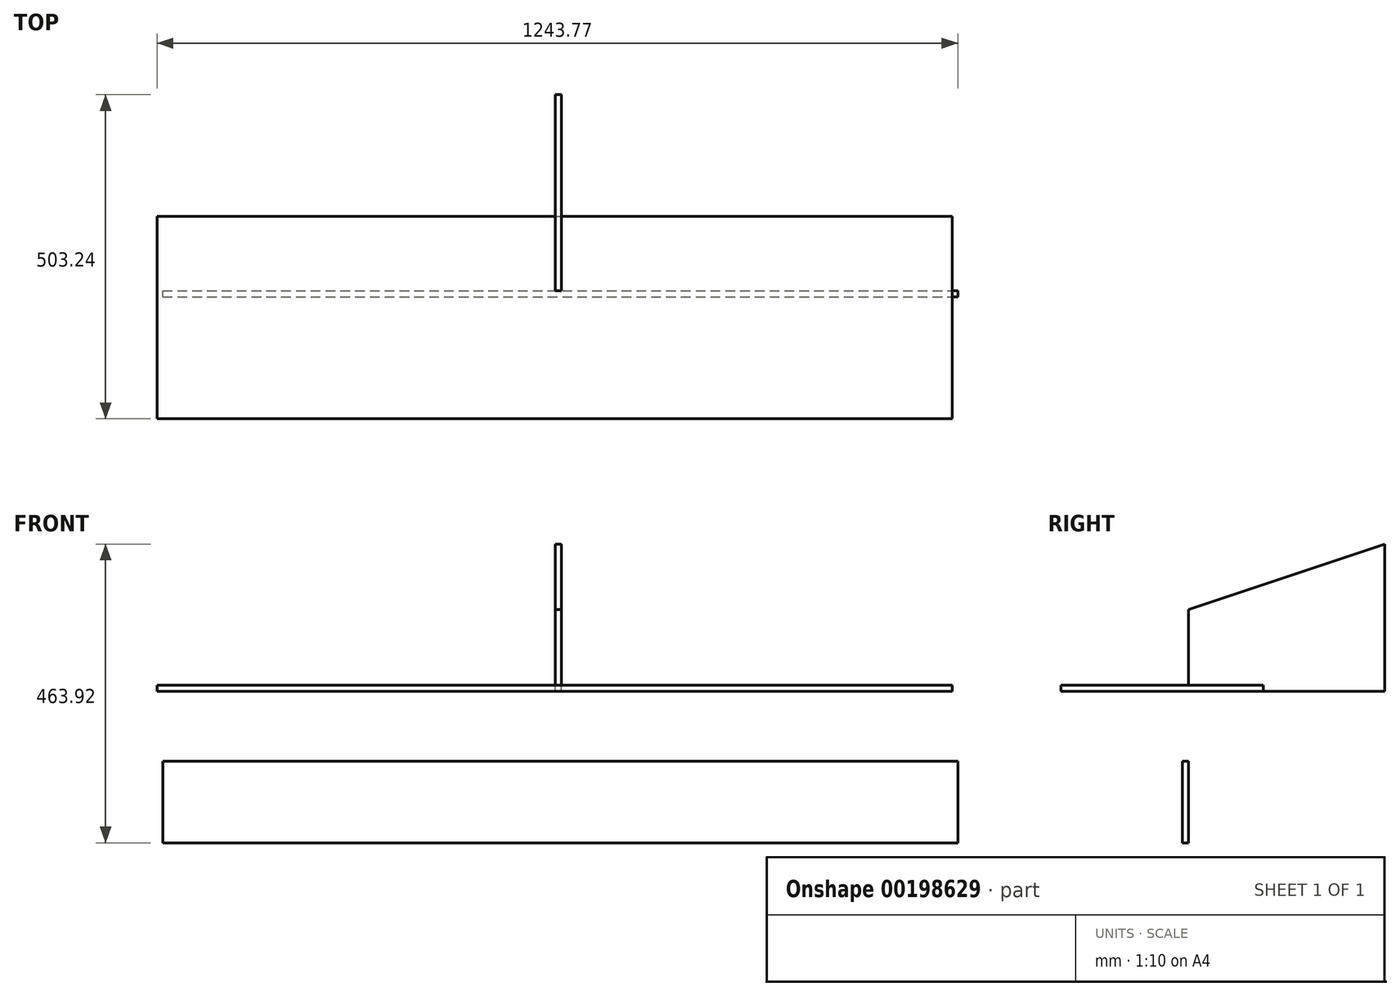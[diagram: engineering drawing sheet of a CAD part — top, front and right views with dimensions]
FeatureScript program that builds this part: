
annotation { "Feature Type Name" : "Feature", "Feature Type Description" : "" }
export const myFeature = defineFeature(function(context is Context, id is Id, definition is map)
    precondition{}
    {
        {
            var Q0;
            Q0=qCreatedBy(makeId("Right.planeOp"),FACE);
            var sketch = newSketch(context, id + "F0", { "sketchPlane" : qUnion([Q0])});
            skLineSegment(sketch, "E0", {"start": v(0, 0) * mm, "end": v(0, 127) * mm});
            skLineSegment(sketch, "E1", {"start": v(0, 0) * mm, "end": v(304.8, 0) * mm});
            skLineSegment(sketch, "E2", {"start": v(304.8, 0) * mm, "end": v(304.8, 228.6) * mm});
            skLineSegment(sketch, "E3", {"start": v(304.8, 228.6) * mm, "end": v(0, 127) * mm});
            skSolve(sketch);
        }
        {
            var Q0;
            Q0 = qSketchRegion(id + "F0", true);
            extrude(context, id + "F1", {"entities" : qUnion([Q0]), "depth" : 9.52 * mm});
        }
        {
            var Q0;
            Q0=qCreatedBy(makeId("Front.planeOp"),FACE);
            var sketch = newSketch(context, id + "F2", { "sketchPlane" : qUnion([Q0])});
            skLineSegment(sketch, "E4.bottom", {"start": v(-609.63, -108.32) * mm, "end": v(625.45, -108.32) * mm});
            skLineSegment(sketch, "E4.top", {"start": v(-609.63, -235.32) * mm, "end": v(625.45, -235.32) * mm});
            skLineSegment(sketch, "E4.left", {"start": v(-609.63, -108.32) * mm, "end": v(-609.63, -235.32) * mm});
            skLineSegment(sketch, "E4.right", {"start": v(625.45, -108.32) * mm, "end": v(625.45, -235.32) * mm});
            skSolve(sketch);
        }
        {
            var Q0;
            Q0 = qSketchRegion(id + "F2", true);
            extrude(context, id + "F3", {"entities" : qUnion([Q0]), "depth" : 9.52 * mm});
        }
        {
            var Q0;
            Q0=qCreatedBy(makeId("Top.planeOp"),FACE);
            var sketch = newSketch(context, id + "F4", { "sketchPlane" : qUnion([Q0])});
            skLineSegment(sketch, "E5", {"start": v(-618.32, 115.89) * mm, "end": v(616.75, 115.89) * mm});
            skLineSegment(sketch, "E6", {"start": v(-618.32, 115.89) * mm, "end": v(-618.32, -198.44) * mm});
            skLineSegment(sketch, "E7", {"start": v(-618.32, -198.44) * mm, "end": v(616.75, -198.44) * mm});
            skLineSegment(sketch, "E8", {"start": v(616.75, -198.44) * mm, "end": v(616.75, 115.89) * mm});
            skLineSegment(sketch, "E9.0", {"start": v(-308.76, 115.89) * mm, "end": v(-308.76, -198.44) * mm});
            skLineSegment(sketch, "E10.0", {"start": v(0.8, 115.89) * mm, "end": v(0.8, -198.44) * mm});
            skLineSegment(sketch, "E11.0", {"start": v(310.37, 115.89) * mm, "end": v(310.37, -198.44) * mm});
            skSolve(sketch);
        }
        {
            var Q0;
            Q0 = qSketchRegion(id + "F4", true);
            extrude(context, id + "F5", {"entities" : qUnion([Q0]), "operationType" : NewBodyOperationType.ADD, "depth" : 9.52 * mm});
        }
        {
            var Q0;
            Q0 = qSketchRegion(id + "F4", true);
            extrude(context, id + "F6", {"entities" : qUnion([Q0]), "depth" : 9.52 * mm});
        }
    });
